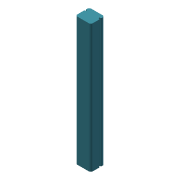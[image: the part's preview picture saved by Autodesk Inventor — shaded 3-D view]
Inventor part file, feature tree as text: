
AUTODESK INVENTOR PART (.ipt)
format: ipt  version: 2014 (Build 180170000, 170)  size: 124,928 bytes
history: native  units: mm
features: other x7, extrude x2, fillet x2, sketch x2, mirror x1
ambient origin geometry x8: Origin, YZ Plane, XZ Plane, XY Plane, X Axis, Y Axis, Z Axis, Center Point
bodies: Solid1 (feature_tree)
feature tree (14):
  other  "Table"
  other  "Rail-01"
  other  "Rail-04"
  other  "Rail-06"
  other  "Rail-05"
  other  "Rail-03"
  other  "Rail-02"
  extrude  "Extrusion1"  Depth=13.5mm
  extrude  "Extrusion2"  Depth=1.0mm
  mirror  "Mirror1"
  fillet  "Fillet1"  Radius=1.0mm
  fillet  "Fillet2"  Radius=0.5mm
  sketch  "Sketch1"  dims[d0=15.0mm d1=13.5mm]
  sketch  "Sketch2"  dims[d2=250.0mm d3=0.0mm d4=4.0mm d5=1.0mm d6=0.5mm d7=0.5mm d8=2.0mm d9=200.0mm d10=0.0mm d11=2.0mm d12=1.0mm]
